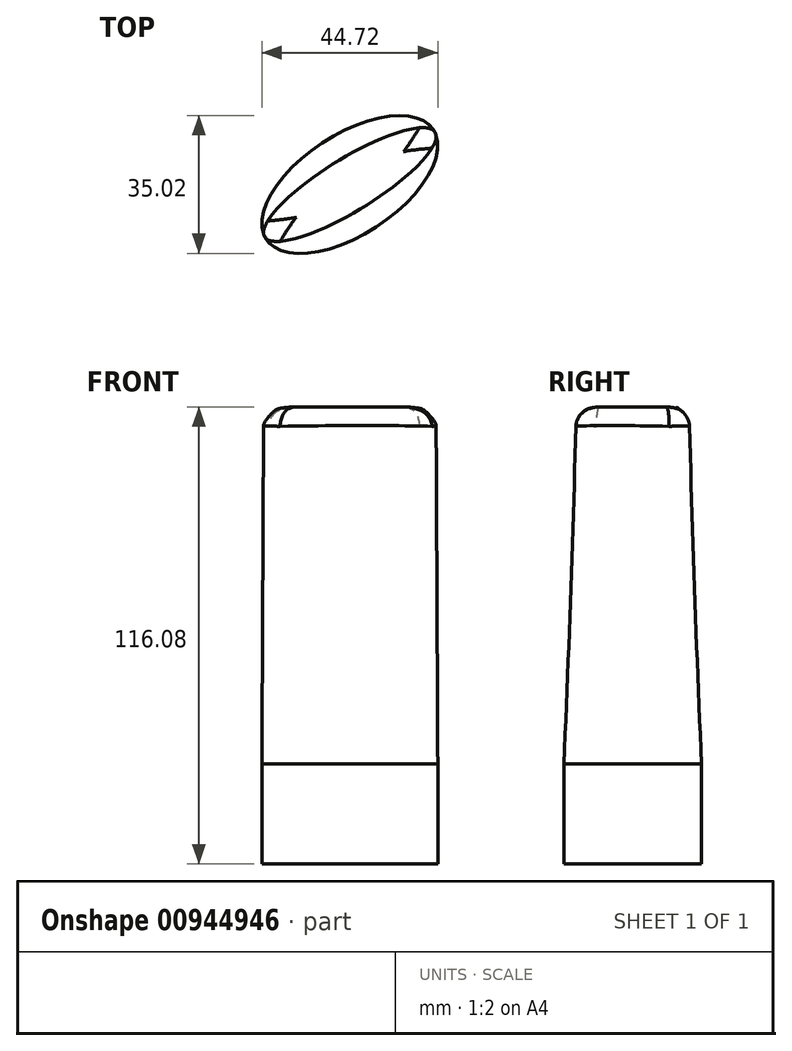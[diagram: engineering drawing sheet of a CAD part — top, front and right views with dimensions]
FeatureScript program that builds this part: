
annotation { "Feature Type Name" : "Feature", "Feature Type Description" : "" }
export const myFeature = defineFeature(function(context is Context, id is Id, definition is map)
    precondition{}
    {
        {
            var Q0;
            Q0=qCreatedBy(makeId("Top.planeOp"),FACE);
            var sketch = newSketch(context, id + "F0", { "sketchPlane" : qUnion([Q0])});
            skEllipse(sketch, "E0", {"center": v(0, 0) * mm, "majorRadius": 25.4 * mm, "minorRadius": 12.7 * mm, "majorAxis": v(0.84, 0.55)});
            skSolve(sketch);
        }
        {
            var Q0;
            Q0=qCreatedBy(makeId("Top.planeOp"),FACE);
            cPlane(context, id + "F1", {"entities" : qUnion([Q0]), "cplaneType" : CPlaneType.OFFSET, "offset" : 90.68 * mm, "width" : 152.4 * mm, "height" : 152.4 * mm});
        }
        {
            var Q0;
            Q0=qCreatedBy(id+"F1.planeOp",FACE);
            var sketch = newSketch(context, id + "F2", { "sketchPlane" : qUnion([Q0])});
            skEllipse(sketch, "E1", {"center": v(0, 0) * mm, "majorRadius": 25.4 * mm, "minorRadius": 6.35 * mm, "majorAxis": v(0.85, 0.52)});
            skSolve(sketch);
        }
        {
            var Q0;
            Q0=makeQuery(id+"F0.imprint","IMPRINT",FACE,{"disambiguationData":[TD([[makeQuery(id+"F0.imprint","IMPRINT",EDGE,{"derivedFrom":sQuery(id+"F0.wireOp",EDGE,"E0")}),1.0]])]});
            var Q1;
            Q1=makeQuery(id+"F2.imprint","IMPRINT",FACE,{"disambiguationData":[TD([[makeQuery(id+"F2.imprint","IMPRINT",EDGE,{"derivedFrom":sQuery(id+"F2.wireOp",EDGE,"E1")}),1.0]])]});
            loft(context, id + "F3", {"sheetProfilesArray" : [{ "sheetProfileEntities" : qUnion([Q0]) }, { "sheetProfileEntities" : qUnion([Q1]) }]});
        }
        {
            var Q0;
            Q0=makeQuery(id+"F3.opLoft","CAP_FACE",FACE,{"disambiguationData":[OSD([makeQuery(id+"F0.imprint","IMPRINT",FACE,{"disambiguationData":[TD([[makeQuery(id+"F0.imprint","IMPRINT",EDGE,{"derivedFrom":sQuery(id+"F0.wireOp",EDGE,"E0")}),1.0]])]})])],"isStart":true});
            extrude(context, id + "F4", {"entities" : qUnion([Q0]), "depth" : 25.4 * mm, "offsetDistance" : 25.4 * mm});
        }
        {
            var Q0;
            Q0=makeQuery(id+"F3.opLoft","MID_CAP_EDGE",EDGE,{"disambiguationData":[OSD([sQuery(id+"F2.wireOp",EDGE,"E1")])],"capPos":1.0});
            fillet(context, id + "F5", {"entities" : qUnion([Q0]), "radius" : 5.08 * mm, "tangentPropagation" : true, "allowEdgeOverflow" : false});
        }
        {
            var Q0;
            Q0=qCreatedBy(makeId("Top.planeOp"),FACE);
            var sketch = newSketch(context, id + "F6", { "sketchPlane" : qUnion([Q0])});
            skLineSegment(sketch, "E2", {"start": v(-30.41, 36.85) * mm, "end": v(42.34, -51.82) * mm});
            skSolve(sketch);
        }
    });
